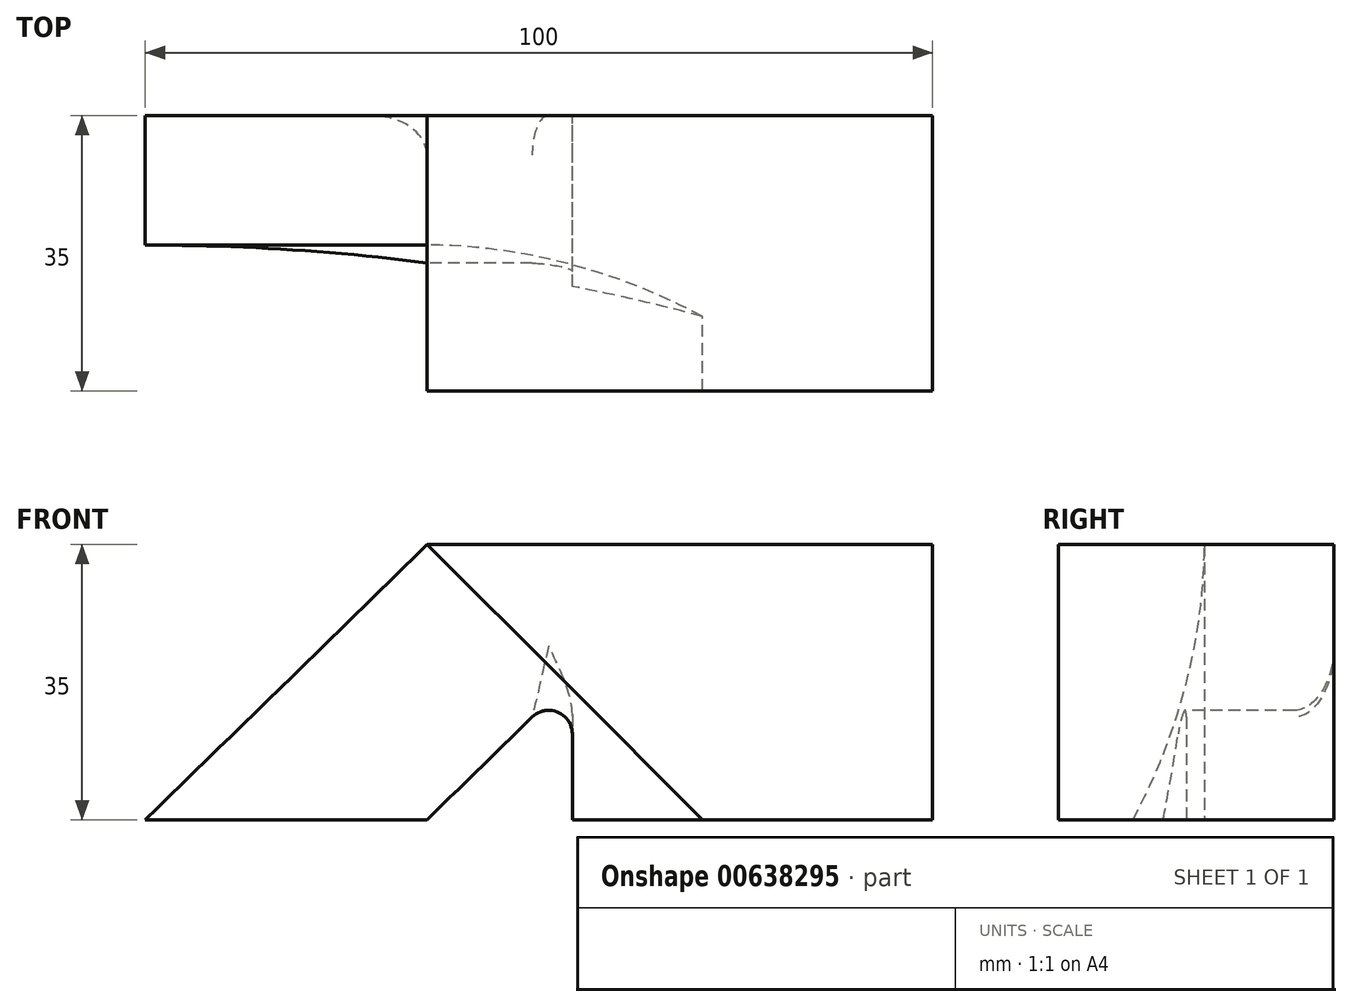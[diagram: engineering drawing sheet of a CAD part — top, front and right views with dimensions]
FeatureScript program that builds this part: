
annotation { "Feature Type Name" : "Feature", "Feature Type Description" : "" }
export const myFeature = defineFeature(function(context is Context, id is Id, definition is map)
    precondition{}
    {
        {
            var Q0;
            Q0=qCreatedBy(makeId("Front.planeOp"),FACE);
            var sketch = newSketch(context, id + "F0", { "sketchPlane" : qUnion([Q0])});
            skLineSegment(sketch, "E0.bottom", {"start": v(0, 0) * mm, "end": v(100, 0) * mm});
            skLineSegment(sketch, "E0.top", {"start": v(0, 35) * mm, "end": v(100, 35) * mm});
            skLineSegment(sketch, "E0.left", {"start": v(0, 0) * mm, "end": v(0, 35) * mm});
            skLineSegment(sketch, "E0.right", {"start": v(100, 0) * mm, "end": v(100, 35) * mm});
            skLineSegment(sketch, "E1", {"start": v(0, 0) * mm, "end": v(49.22, 48.09) * mm});
            skLineSegment(sketch, "E2.0", {"start": v(16.45, -18.88) * mm, "end": v(54.25, 18.06) * mm});
            skLineSegment(sketch, "E3", {"start": v(54.25, 18.06) * mm, "end": v(54.25, -28.07) * mm});
            skSolve(sketch);
        }
        {
            var Q0;
            {var subQ0=sQuery(id+"F0.wireOp",EDGE,"E0.right");Q0=makeQuery(id+"F0.imprint","IMPRINT",FACE,{"disambiguationData":[TD([[makeQuery(id+"F0.imprint","IMPRINT",EDGE,{"derivedFrom":subQ0}),1.0]])]});}
            extrude(context, id + "F1", {"entities" : qUnion([Q0]), "endBound" : BoundingType.SYMMETRIC, "depth" : 35 * mm, "offsetDistance" : 25 * mm});
        }
        {
            var Q0;
            Q0=makeQuery(id+"F1.opExtrude","CAP_EDGE",EDGE,{"disambiguationData":[OSD([sQuery(id+"F0.wireOp",EDGE,"E2.0")])],"isStart":false});
            var Q1;
            Q1=makeQuery(id+"F1.opExtrude","CAP_EDGE",EDGE,{"disambiguationData":[OSD([sQuery(id+"F0.wireOp",EDGE,"E2.0")])],"isStart":true});
            fillet(context, id + "F2", {"entities" : qUnion([Q0, Q1]), "radius" : 5 * mm, "tangentPropagation" : true, "allowEdgeOverflow" : false});
        }
        {
            var Q0;
            Q0=makeQuery(id+"F1.opExtrude","SWEPT_EDGE",EDGE,{"disambiguationData":[OSD([sQuery(id+"F0.wireOp",EDGE,"E0.top"),sQuery(id+"F0.wireOp",EDGE,"E1")])]});
            cPlane(context, id + "F3", {"entities" : qUnion([Q0]), "cplaneType" : CPlaneType.LINE_ANGLE, "offset" : 25 * mm, "angle" : 45 * degree, "width" : 150 * mm, "height" : 150 * mm});
        }
        {
            var Q0;
            Q0=qCreatedBy(id+"F3.planeOp",FACE);
            var sketch = newSketch(context, id + "F4", { "sketchPlane" : qUnion([Q0])});
            skCircle(sketch, "E4", {"center": v(-141.6, 0) * mm, "radius": 142.64 * mm});
            skSolve(sketch);
        }
        {
            var Q0;
            Q0 = qSketchRegion(id + "F4", true);
            extrude(context, id + "F5", {"entities" : qUnion([Q0]), "operationType" : NewBodyOperationType.REMOVE, "endBound" : BoundingType.THROUGH_ALL, "oppositeDirection" : true, "depth" : 25 * mm, "offsetDistance" : 25 * mm});
        }
        {
            var Q0;
            Q0=makeQuery(id+"F1.opExtrude","SWEPT_EDGE",EDGE,{"disambiguationData":[OSD([sQuery(id+"F0.wireOp",EDGE,"E2.0"),sQuery(id+"F0.wireOp",EDGE,"E3")])]});
            fillet(context, id + "F6", {"entities" : qUnion([Q0]), "radius" : 3 * mm, "tangentPropagation" : true, "allowEdgeOverflow" : false});
        }
    });
